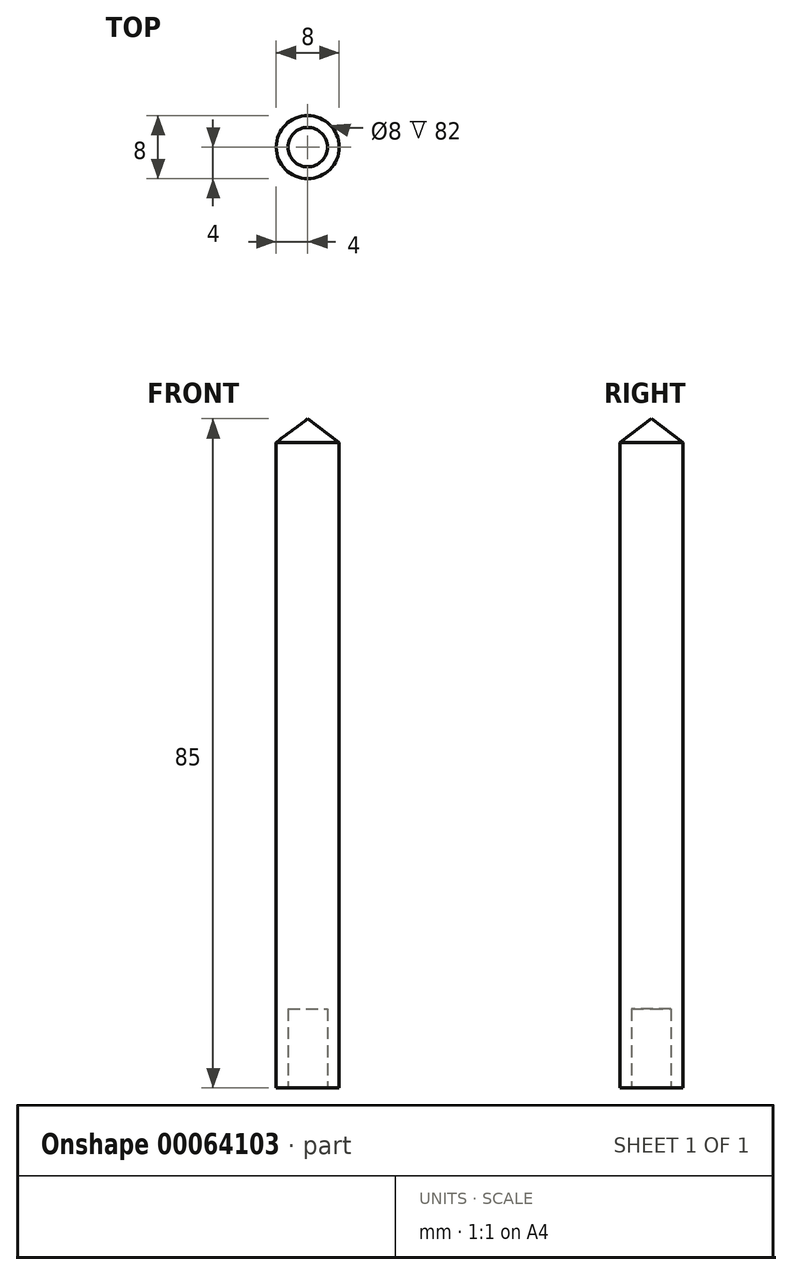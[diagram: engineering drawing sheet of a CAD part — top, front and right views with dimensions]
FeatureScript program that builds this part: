
annotation { "Feature Type Name" : "Feature", "Feature Type Description" : "" }
export const myFeature = defineFeature(function(context is Context, id is Id, definition is map)
    precondition{}
    {
        {
            var Q0;
            Q0=qCreatedBy(makeId("Front.planeOp"),FACE);
            var sketch = newSketch(context, id + "F0", { "sketchPlane" : qUnion([Q0])});
            skLineSegment(sketch, "E0", {"start": v(0, 0) * mm, "end": v(-4, -3) * mm});
            skLineSegment(sketch, "E1", {"start": v(-4, -3) * mm, "end": v(-4, -85) * mm});
            skLineSegment(sketch, "E2", {"start": v(-4, -85) * mm, "end": v(-2.5, -85) * mm});
            skLineSegment(sketch, "E3", {"start": v(-2.5, -85) * mm, "end": v(-2.5, -75) * mm});
            skLineSegment(sketch, "E4", {"start": v(-2.5, -75) * mm, "end": v(0, -75) * mm});
            skSolve(sketch);
        }
        {
            var Q0;
            Q0=qCreatedBy(makeId("Front.planeOp"),FACE);
            var sketch = newSketch(context, id + "F1", { "sketchPlane" : qUnion([Q0])});
            skLineSegment(sketch, "E5", {"start": v(0, 0) * mm, "end": v(0, -91.66) * mm, "construction": true});
            skSolve(sketch);
        }
        {
            var Q0;
            Q0=sQuery(id+"F0.wireOp",EDGE,"E0");
            var Q1;
            Q1=sQuery(id+"F0.wireOp",EDGE,"E1");
            var Q2;
            Q2=sQuery(id+"F0.wireOp",EDGE,"E2");
            var Q3;
            Q3=sQuery(id+"F0.wireOp",EDGE,"E3");
            var Q4;
            Q4=sQuery(id+"F0.wireOp",EDGE,"E4");
            var Q5;
            Q5=sQuery(id+"F1.wireOp",EDGE,"E5");
            revolve(context, id + "F2", {"bodyType" : ToolBodyType.SURFACE, "surfaceEntities" : qUnion([Q0, Q1, Q2, Q3, Q4]), "axis" : qUnion([Q5]), "revolveType" : RevolveType.FULL});
        }
    });
